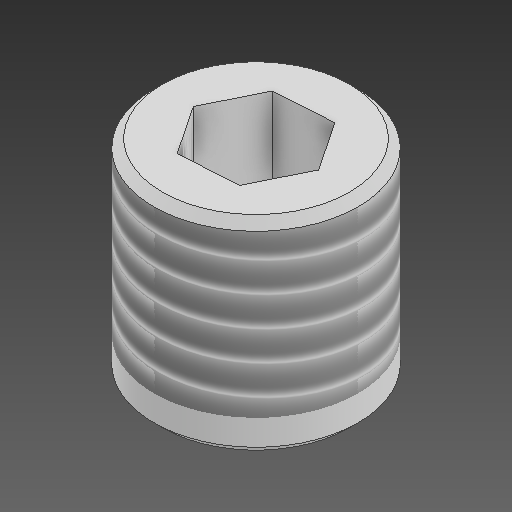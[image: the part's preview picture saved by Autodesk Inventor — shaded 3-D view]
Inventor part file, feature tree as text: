
AUTODESK INVENTOR PART (.ipt)
format: ipt  version: 2021 (Build 250183000, 183)  size: 172,544 bytes
history: native  units: mm
features: extrude x2, sketch x2, thread x1, chamfer x1
ambient origin geometry x8: Origin, YZ Plane, XZ Plane, XY Plane, X Axis, Y Axis, Z Axis, Center Point
bodies: Solid1 (feature_tree)
feature tree (6):
  extrude  "Extrusion1"  Depth=6.0mm
  extrude  "Extrusion2"  Depth=5.5mm TaperAngle=0.0deg
  thread  "Thread1"  [1 undecoded]
  chamfer  "Chamfer1"  Distance=0.5mm Angle=45.0deg
  sketch  "Sketch1"  dims[d0=12.0mm d1=0.0mm d2=6.0mm]
  sketch  "Sketch2"  dims[d3=12.0mm d4=5.5mm d5=0.0mm d6=10.0mm d7=0.0mm d8=0.5mm d9=2.0mm d10=45.0deg]
note: 1 required parameter value undecoded (feature->parameter linkage not recoverable at this tier; creation-order binding heuristic only, values carry confidence <= 0.55)
